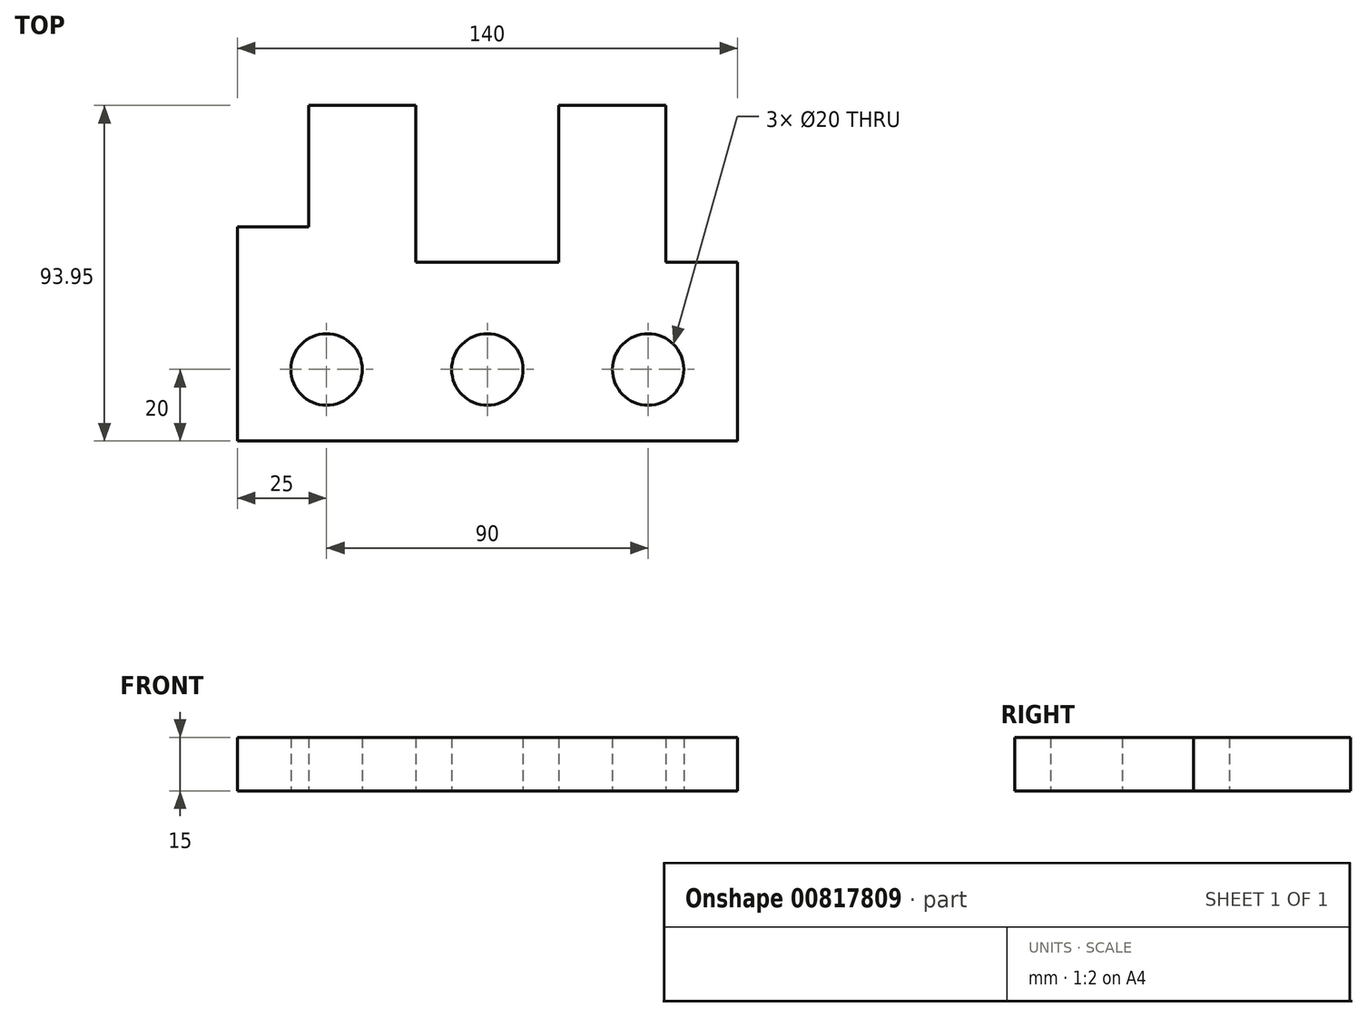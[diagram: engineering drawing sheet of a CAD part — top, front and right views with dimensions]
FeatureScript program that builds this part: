
annotation { "Feature Type Name" : "Feature", "Feature Type Description" : "" }
export const myFeature = defineFeature(function(context is Context, id is Id, definition is map)
    precondition{}
    {
        {
            var Q0;
            Q0=qCreatedBy(makeId("Top.planeOp"),FACE);
            var sketch = newSketch(context, id + "F0", { "sketchPlane" : qUnion([Q0])});
            skLineSegment(sketch, "E0", {"start": v(0, 0) * mm, "end": v(0, 50) * mm});
            skLineSegment(sketch, "E1", {"start": v(0, 50) * mm, "end": v(-20, 50) * mm});
            skLineSegment(sketch, "E2", {"start": v(-20, 50) * mm, "end": v(-20, 93.95) * mm});
            skLineSegment(sketch, "E3", {"start": v(-20, 93.95) * mm, "end": v(-50, 93.95) * mm});
            skLineSegment(sketch, "E4", {"start": v(-50, 93.95) * mm, "end": v(-50, 50) * mm});
            skLineSegment(sketch, "E5", {"start": v(-50, 50) * mm, "end": v(-90, 50) * mm});
            skLineSegment(sketch, "E6", {"start": v(-90, 50) * mm, "end": v(-90, 93.95) * mm});
            skLineSegment(sketch, "E7", {"start": v(-90, 93.95) * mm, "end": v(-120, 93.95) * mm});
            skLineSegment(sketch, "E8", {"start": v(-120, 93.95) * mm, "end": v(-120, 60) * mm});
            skLineSegment(sketch, "E9", {"start": v(-120, 60) * mm, "end": v(-140, 60) * mm});
            skLineSegment(sketch, "E10", {"start": v(-140, 60) * mm, "end": v(-140, 0) * mm});
            skLineSegment(sketch, "E11", {"start": v(-140, 0) * mm, "end": v(0, 0) * mm});
            skCircle(sketch, "E12", {"center": v(-115, 20) * mm, "radius": 10 * mm});
            skCircle(sketch, "E13", {"center": v(-70, 20) * mm, "radius": 10 * mm});
            skCircle(sketch, "E14", {"center": v(-25, 20) * mm, "radius": 10 * mm});
            skSolve(sketch);
        }
        {
            var Q0;
            Q0=makeQuery(id+"F0.imprint","IMPRINT",FACE,{"disambiguationData":[TD([[makeQuery(id+"F0.imprint","IMPRINT",EDGE,{"derivedFrom":sQuery(id+"F0.wireOp",EDGE,"E0")}),1.0]])]});
            extrude(context, id + "F1", {"entities" : qUnion([Q0]), "depth" : 15 * mm, "offsetDistance" : 25 * mm});
        }
    });
